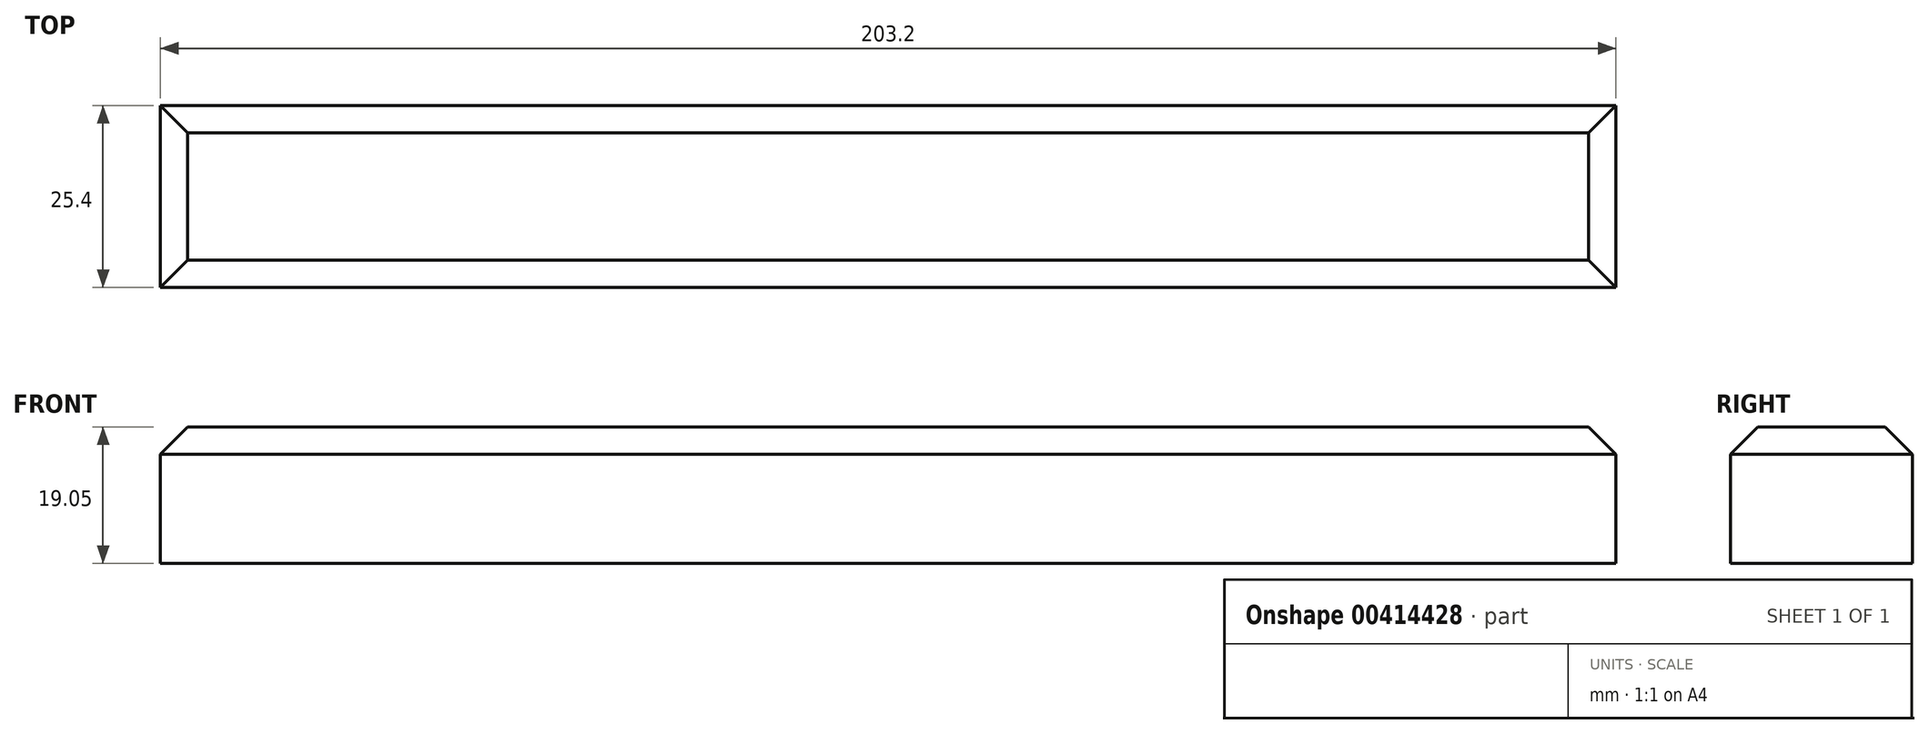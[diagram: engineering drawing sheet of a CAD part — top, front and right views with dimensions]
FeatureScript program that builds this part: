
annotation { "Feature Type Name" : "Feature", "Feature Type Description" : "" }
export const myFeature = defineFeature(function(context is Context, id is Id, definition is map)
    precondition{}
    {
        {
            var Q0;
            Q0=qCreatedBy(makeId("Top.planeOp"),FACE);
            var sketch = newSketch(context, id + "F0", { "sketchPlane" : qUnion([Q0])});
            skLineSegment(sketch, "E0.bottom", {"start": v(-96.85, -3.1) * mm, "end": v(106.35, -3.1) * mm});
            skLineSegment(sketch, "E0.top", {"start": v(-96.85, -28.5) * mm, "end": v(106.35, -28.5) * mm});
            skLineSegment(sketch, "E0.left", {"start": v(-96.85, -3.1) * mm, "end": v(-96.85, -28.5) * mm});
            skLineSegment(sketch, "E0.right", {"start": v(106.35, -3.1) * mm, "end": v(106.35, -28.5) * mm});
            skSolve(sketch);
        }
        {
            var Q0;
            Q0=makeQuery(id+"F0.imprint","IMPRINT",FACE,{"disambiguationData":[TD([[makeQuery(id+"F0.imprint","IMPRINT",EDGE,{"derivedFrom":sQuery(id+"F0.wireOp",EDGE,"E0.bottom")}),-1.0]])]});
            extrude(context, id + "F1", {"entities" : qUnion([Q0]), "depth" : 19.05 * mm});
        }
        {
            var Q0;
            Q0=makeQuery(id+"F1.opExtrude","CAP_EDGE",EDGE,{"disambiguationData":[OSD([sQuery(id+"F0.wireOp",EDGE,"E0.left")])],"isStart":false});
            var Q1;
            Q1=makeQuery(id+"F1.opExtrude","CAP_EDGE",EDGE,{"disambiguationData":[OSD([sQuery(id+"F0.wireOp",EDGE,"E0.right")])],"isStart":false});
            var Q2;
            Q2=makeQuery(id+"F1.opExtrude","CAP_EDGE",EDGE,{"disambiguationData":[OSD([sQuery(id+"F0.wireOp",EDGE,"E0.top")])],"isStart":false});
            var Q3;
            Q3=makeQuery(id+"F1.opExtrude","CAP_EDGE",EDGE,{"disambiguationData":[OSD([sQuery(id+"F0.wireOp",EDGE,"E0.bottom")])],"isStart":false});
            chamfer(context, id + "F2", {"entities" : qUnion([Q0, Q1, Q2, Q3]), "width" : 3.8 * mm, "tangentPropagation" : true});
        }
    });
